FREECAD ASSEMBLY — COMPONENT RECIPES ("barrel")

This assembly document has 8 components, labeled P0..P7 below (a component is one placed body or linked part). 0 of them carry a construction recipe — the FreeCAD feature program that regenerates the part from scratch, quoted from this document or its linked companion documents; the rest are supplied as boundary geometry only. No exploded tour is included for this assembly.
COMPONENT P0 — geometry summary ("Body"; no construction recipe available for this part):
  bounding box: 80.0 x 80.0 x 15.0 mm
  tessellated surface: 32,448 triangles
  volume: 12159 mm^3 (13% of its bounding box)
  symmetry: 2-fold rotationally symmetric about the x axis
COMPONENT P1 — geometry summary ("Spacer1"; no construction recipe available for this part):
  bounding box: 55.0 x 8.0 x 8.0 mm
  tessellated surface: 1,008 triangles
  volume: 2376 mm^3 (68% of its bounding box)
  symmetry: revolution-symmetric about the x axis through its bounding-box center; 2-fold rotationally symmetric about the y axis; 2-fold rotationally symmetric about the z axis; mirror-symmetric across its x mid-plane
COMPONENT P2 — geometry summary ("Spacer2"; no construction recipe available for this part):
  bounding box: 55.0 x 8.0 x 8.0 mm
  tessellated surface: 1,008 triangles
  volume: 2376 mm^3 (68% of its bounding box)
  symmetry: revolution-symmetric about the x axis through its bounding-box center; 2-fold rotationally symmetric about the y axis; 2-fold rotationally symmetric about the z axis; mirror-symmetric across its x mid-plane
COMPONENT P3 — geometry summary ("Spacer3"; no construction recipe available for this part):
  bounding box: 55.0 x 8.0 x 8.0 mm
  tessellated surface: 1,008 triangles
  volume: 2376 mm^3 (68% of its bounding box)
  symmetry: revolution-symmetric about the x axis through its bounding-box center; 2-fold rotationally symmetric about the y axis; 2-fold rotationally symmetric about the z axis; mirror-symmetric across its x mid-plane
COMPONENT P4 — geometry summary ("Spacer4"; no construction recipe available for this part):
  bounding box: 55.0 x 8.0 x 8.0 mm
  tessellated surface: 1,008 triangles
  volume: 2376 mm^3 (68% of its bounding box)
  symmetry: revolution-symmetric about the x axis through its bounding-box center; 2-fold rotationally symmetric about the y axis; 2-fold rotationally symmetric about the z axis; mirror-symmetric across its x mid-plane
COMPONENT P5 — geometry summary ("SideOpen"; no construction recipe available for this part):
  bounding box: 80.0 x 80.0 x 3.0 mm
  tessellated surface: 28,948 triangles
  volume: 6329 mm^3 (33% of its bounding box)
  symmetry: mirror-symmetric across its x mid-plane
COMPONENT P6 — geometry summary ("Flap2"; no construction recipe available for this part):
  bounding box: 62.0 x 40.0 x 3.5 mm
  tessellated surface: 588 triangles
  volume: 2166 mm^3 (25% of its bounding box)
  symmetry: mirror-symmetric across its x mid-plane
COMPONENT P7 — geometry summary ("Flap1"; no construction recipe available for this part):
  bounding box: 62.0 x 40.0 x 2.5 mm
  tessellated surface: 588 triangles
  volume: 2166 mm^3 (35% of its bounding box)
  symmetry: mirror-symmetric across its x mid-plane
PROVENANCE & LICENSES
A FreeCAD (.FCStd) document from a public repository crawl; recipes are the document's own serialized feature recipes (and, for linked parts, companion documents' recipes).
License: mit.
